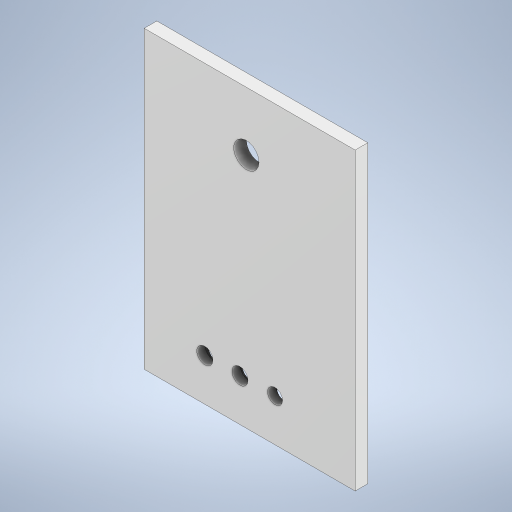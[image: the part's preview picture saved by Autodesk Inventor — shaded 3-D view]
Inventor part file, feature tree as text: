
AUTODESK INVENTOR PART (.ipt)
format: ipt  version: 2023 (Build 270158000, 158)  size: 249,344 bytes
history: native  units: mm
features: sketch x7, hole x5, extrude x2
ambient origin geometry x8: Origin, YZ Plane, XZ Plane, XY Plane, X Axis, Y Axis, Z Axis, Center Point
bodies: Solid1 (feature_tree)
feature tree (14):
  extrude  "Extrusion1"  Depth=350.0mm
  extrude  "Extrusion2"  Depth=10.0mm TaperAngle=0.0deg
  hole  "Hole1"  [1 undecoded]
  hole  "Hole2"  [1 undecoded]
  hole  "Hole3"  [1 undecoded]
  hole  "Hole4"  [1 undecoded]
  hole  "Hole5"  [1 undecoded]
  sketch  "Sketch1"  dims[d0=250.0mm d1=350.0mm]
  sketch  "Sketch2"  dims[d2=15.0mm d3=0.0mm d18=10.0mm d19=0.0mm]
  sketch  "Sketch3"  dims[d20=20.0mm d21=6.0mm d22=4.0mm d23=2.0mm d24=90.0deg d25=8.0mm d26=20.594885mm]
  sketch  "Sketch4"  dims[d27=20.0mm d28=6.0mm d29=4.0mm d30=2.0mm d31=90.0deg d32=8.0mm d33=20.594885mm]
  sketch  "Sketch5"  dims[d34=20.0mm d35=6.0mm d36=4.0mm d37=2.0mm d38=90.0deg d39=8.0mm d40=20.594885mm d41=20.0mm]
  sketch  "Sketch6"  dims[d42=20.0mm d43=6.0mm d44=4.0mm d45=2.0mm d46=90.0deg d47=8.0mm d48=20.594885mm d49=30.0mm]
  sketch  "Sketch7"  dims[d50=30.0mm d51=6.0mm d52=4.0mm d53=2.0mm d54=90.0deg d55=8.0mm d56=20.594885mm]
note: 5 required parameter values undecoded (feature->parameter linkage not recoverable at this tier; creation-order binding heuristic only, values carry confidence <= 0.55)
